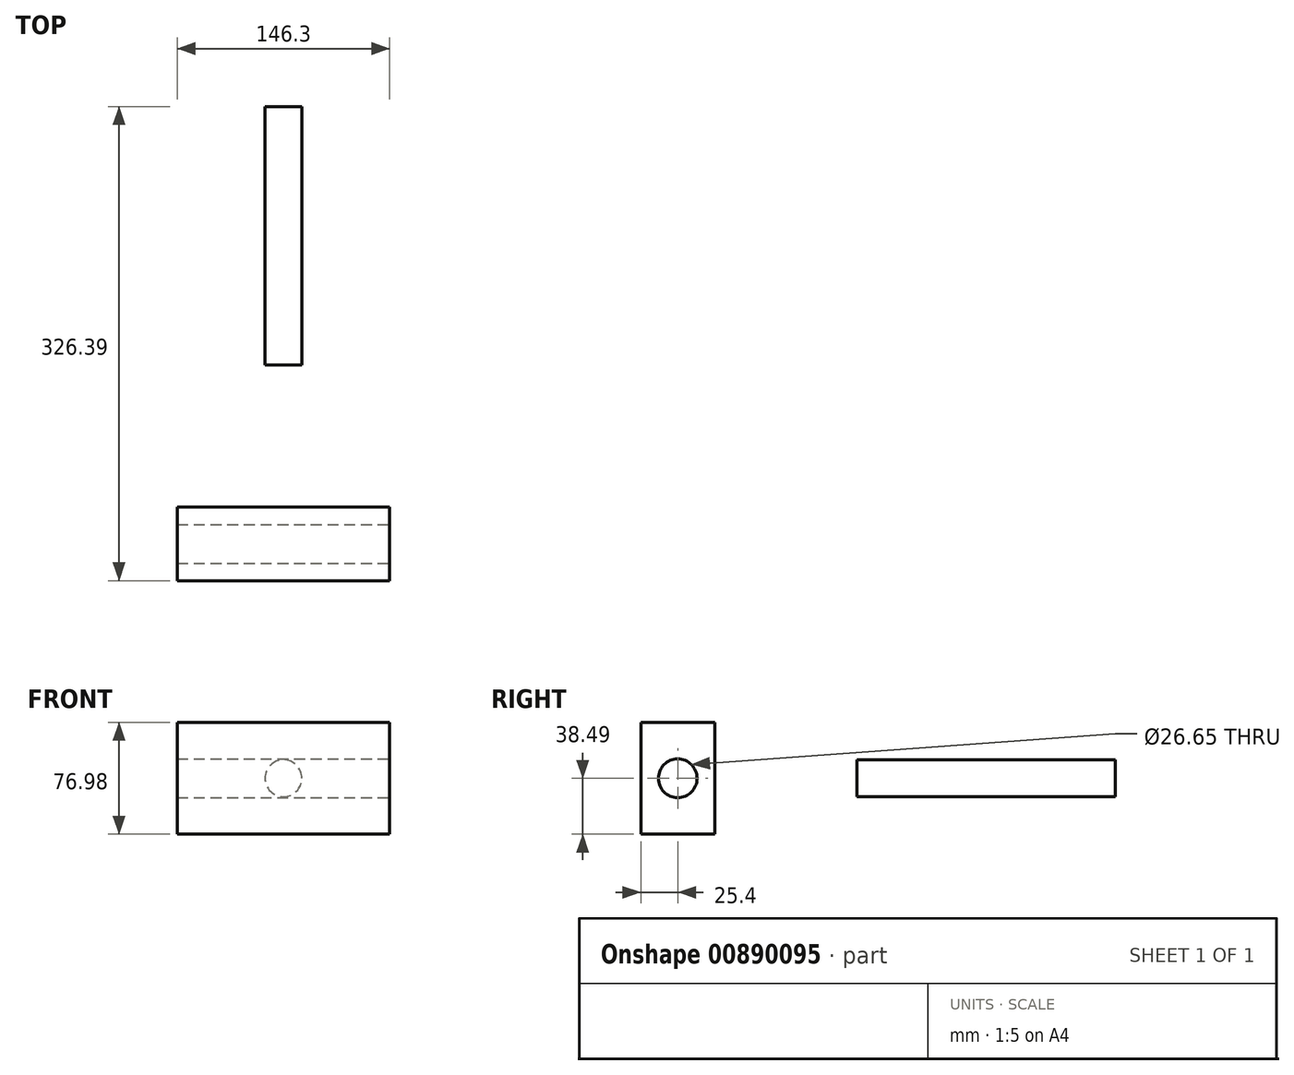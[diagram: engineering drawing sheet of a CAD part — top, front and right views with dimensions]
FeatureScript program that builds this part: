
annotation { "Feature Type Name" : "Feature", "Feature Type Description" : "" }
export const myFeature = defineFeature(function(context is Context, id is Id, definition is map)
    precondition{}
    {
        {
            var Q0;
            Q0=qCreatedBy(makeId("Front.planeOp"),FACE);
            var sketch = newSketch(context, id + "F0", { "sketchPlane" : qUnion([Q0])});
            skLineSegment(sketch, "E0.bottom", {"start": v(73.15, -38.5) * mm, "end": v(-73.15, -38.5) * mm});
            skLineSegment(sketch, "E0.top", {"start": v(73.15, 38.5) * mm, "end": v(-73.15, 38.5) * mm});
            skLineSegment(sketch, "E0.left", {"start": v(73.15, -38.5) * mm, "end": v(73.15, 38.5) * mm});
            skLineSegment(sketch, "E0.right", {"start": v(-73.15, -38.5) * mm, "end": v(-73.15, 38.5) * mm});
            skPoint(sketch, "E0.middle", {"position": v(0, 0) * mm});
            skSolve(sketch);
        }
        {
            var Q0;
            Q0 = qSketchRegion(id + "F0", true);
            extrude(context, id + "F1", {"entities" : qUnion([Q0]), "depth" : 50.8 * mm, "offsetDistance" : 25.4 * mm});
        }
        {
            var Q0;
            Q0=makeQuery(id+"F1.opExtrude","SWEPT_FACE",FACE,{"disambiguationData":[OSD([sQuery(id+"F0.wireOp",EDGE,"E0.left")])]});
            var sketch = newSketch(context, id + "F2", { "sketchPlane" : qUnion([Q0])});
            skCircle(sketch, "E1", {"center": v(-25.4, 0) * mm, "radius": 13.32 * mm});
            skSolve(sketch);
        }
        {
            var Q0;
            Q0=makeQuery(id+"F2.imprint","IMPRINT",FACE,{"disambiguationData":[TD([[makeQuery(id+"F2.imprint","IMPRINT",EDGE,{"derivedFrom":sQuery(id+"F2.wireOp",EDGE,"E1")}),1.0]])]});
            var Q1;
            Q1=sQuery(id+"F2.wireOp",EDGE,"E1");
            extrude(context, id + "F3", {"entities" : qUnion([Q0]), "operationType" : NewBodyOperationType.REMOVE, "surfaceEntities" : qUnion([Q1]), "oppositeDirection" : true, "depth" : 228.6 * mm, "offsetDistance" : 25.4 * mm});
        }
        {
            var Q0;
            Q0=qCreatedBy(makeId("Front.planeOp"),FACE);
            cPlane(context, id + "F4", {"entities" : qUnion([Q0]), "cplaneType" : CPlaneType.OFFSET, "offset" : 275.59 * mm, "oppositeDirection" : true, "width" : 152.4 * mm, "height" : 152.4 * mm});
        }
        {
            var Q0;
            Q0=qCreatedBy(id+"F4.planeOp",FACE);
            var sketch = newSketch(context, id + "F5", { "sketchPlane" : qUnion([Q0])});
            skCircle(sketch, "E2", {"center": v(0, 0) * mm, "radius": 12.7 * mm});
            skSolve(sketch);
        }
        {
            var Q0;
            Q0 = qSketchRegion(id + "F5", true);
            extrude(context, id + "F6", {"entities" : qUnion([Q0]), "depth" : 177.8 * mm, "offsetDistance" : 25.4 * mm});
        }
    });
